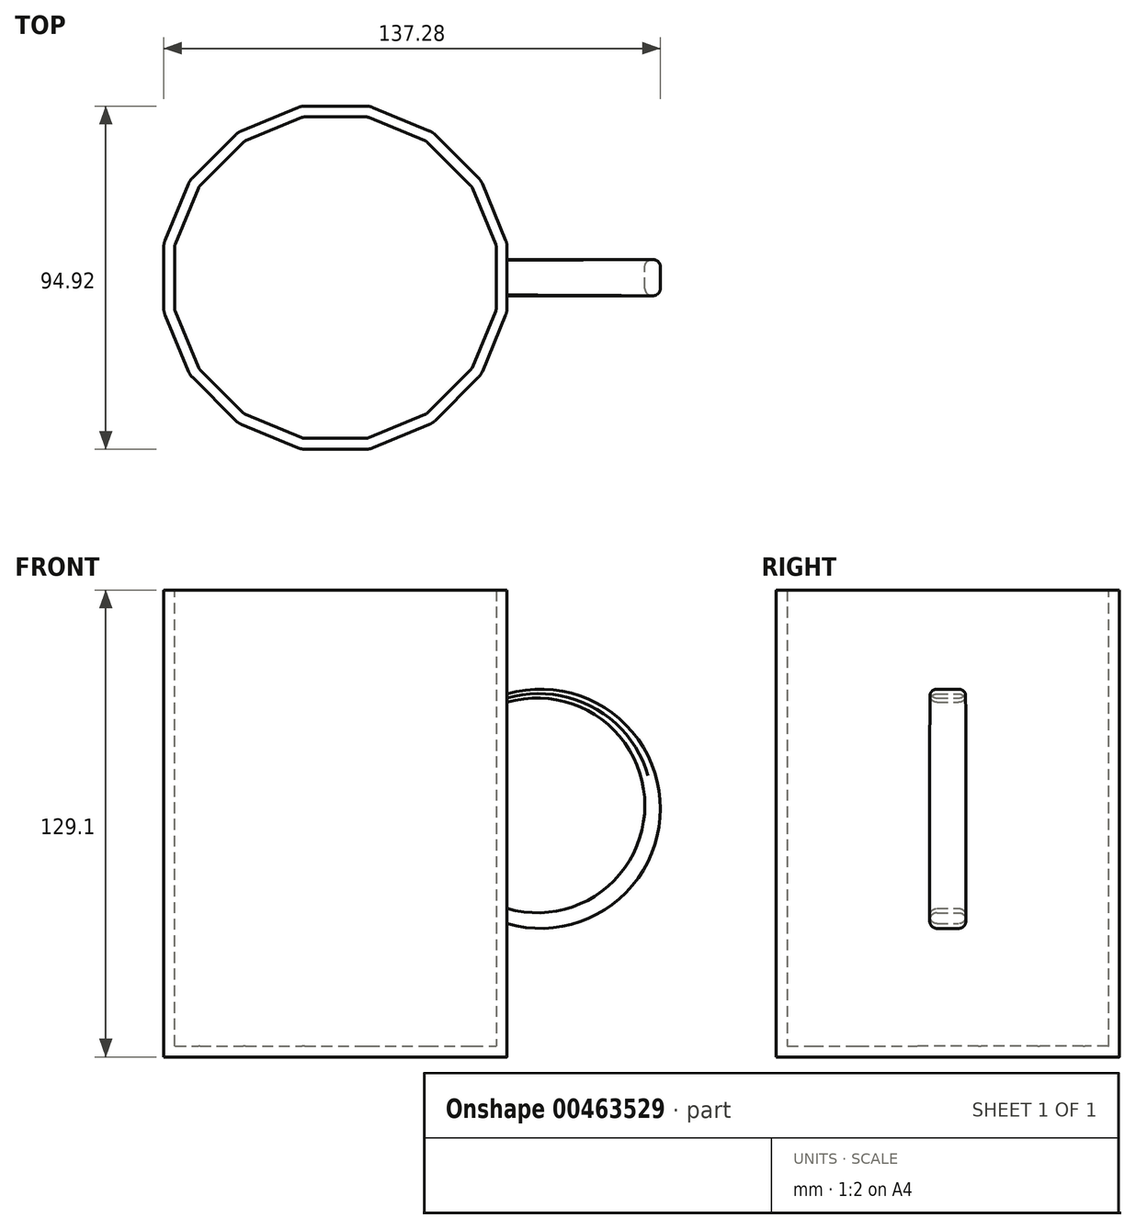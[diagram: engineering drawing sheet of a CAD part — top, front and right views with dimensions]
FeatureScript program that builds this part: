
annotation { "Feature Type Name" : "Feature", "Feature Type Description" : "" }
export const myFeature = defineFeature(function(context is Context, id is Id, definition is map)
    precondition{}
    {
        {
            var Q0;
            Q0=qCreatedBy(makeId("Front.planeOp"),FACE);
            var sketch = newSketch(context, id + "F0", { "sketchPlane" : qUnion([Q0])});
            skArc(sketch, "E0", {"start": v(45.81, 37.4) * mm, "mid": v(89.82, 68.9) * mm, "end": v(45.32, 99.7) * mm});
            skArc(sketch, "E1", {"start": v(46, 41.55) * mm, "mid": v(85.52, 69.91) * mm, "end": v(45.37, 97.38) * mm});
            skLineSegment(sketch, "E2", {"start": v(45.32, 99.7) * mm, "end": v(45.37, 97.38) * mm});
            skLineSegment(sketch, "E3", {"start": v(46, 41.55) * mm, "end": v(45.81, 37.4) * mm});
            skSolve(sketch);
        }
        {
            var Q0;
            Q0=makeQuery(id+"F0.imprint","IMPRINT",FACE,{"disambiguationData":[TD([[makeQuery(id+"F0.imprint","IMPRINT",EDGE,{"derivedFrom":sQuery(id+"F0.wireOp",EDGE,"E0")}),1.0]])]});
            extrude(context, id + "F1", {"entities" : qUnion([Q0]), "endBound" : BoundingType.SYMMETRIC, "depth" : 10 * mm});
        }
        {
            var Q0;
            Q0=qCreatedBy(makeId("Top.planeOp"),FACE);
            var sketch = newSketch(context, id + "F2", { "sketchPlane" : qUnion([Q0])});
            skCircle(sketch, "E4.cCircle", {"center": v(0, 0) * mm, "radius": 47.46 * mm, "construction": true});
            skLineSegment(sketch, "E4.0", {"start": v(47.46, 9.44) * mm, "end": v(47.46, -9.44) * mm});
            skLineSegment(sketch, "E4.1", {"start": v(47.46, -9.44) * mm, "end": v(40.23, -26.88) * mm});
            skLineSegment(sketch, "E4.2", {"start": v(40.23, -26.88) * mm, "end": v(26.88, -40.23) * mm});
            skLineSegment(sketch, "E4.3", {"start": v(26.88, -40.23) * mm, "end": v(9.44, -47.46) * mm});
            skLineSegment(sketch, "E4.4", {"start": v(9.44, -47.46) * mm, "end": v(-9.44, -47.46) * mm});
            skLineSegment(sketch, "E4.5", {"start": v(-9.44, -47.46) * mm, "end": v(-26.88, -40.23) * mm});
            skLineSegment(sketch, "E4.6", {"start": v(-26.88, -40.23) * mm, "end": v(-40.23, -26.88) * mm});
            skLineSegment(sketch, "E4.7", {"start": v(-40.23, -26.88) * mm, "end": v(-47.46, -9.44) * mm});
            skLineSegment(sketch, "E4.8", {"start": v(-47.46, -9.44) * mm, "end": v(-47.46, 9.44) * mm});
            skLineSegment(sketch, "E4.9", {"start": v(-47.46, 9.44) * mm, "end": v(-40.23, 26.88) * mm});
            skLineSegment(sketch, "E4.10", {"start": v(-40.23, 26.88) * mm, "end": v(-26.88, 40.23) * mm});
            skLineSegment(sketch, "E4.11", {"start": v(-26.88, 40.23) * mm, "end": v(-9.44, 47.46) * mm});
            skLineSegment(sketch, "E4.12", {"start": v(-9.44, 47.46) * mm, "end": v(9.44, 47.46) * mm});
            skLineSegment(sketch, "E4.13", {"start": v(9.44, 47.46) * mm, "end": v(26.88, 40.23) * mm});
            skLineSegment(sketch, "E4.14", {"start": v(26.88, 40.23) * mm, "end": v(40.23, 26.88) * mm});
            skLineSegment(sketch, "E4.15", {"start": v(40.23, 26.88) * mm, "end": v(47.46, 9.44) * mm});
            skPoint(sketch, "E4.0.midPoint", {"position": v(47.46, 0) * mm});
            skSolve(sketch);
        }
        {
            var Q0;
            Q0=makeQuery(id+"F2.imprint","IMPRINT",FACE,{"disambiguationData":[TD([[makeQuery(id+"F2.imprint","IMPRINT",EDGE,{"derivedFrom":sQuery(id+"F2.wireOp",EDGE,"E4.0")}),-1.0]])]});
            extrude(context, id + "F3", {"entities" : qUnion([Q0]), "operationType" : NewBodyOperationType.ADD, "depth" : 129.1 * mm});
        }
        {
            var Q0;
            Q0=makeQuery(id+"F3.opExtrude","SWEPT_EDGE",EDGE,{"disambiguationData":[OSD([sQuery(id+"F2.wireOp",EDGE,"E4.6"),sQuery(id+"F2.wireOp",EDGE,"E4.7")])]});
            var Q1;
            Q1=makeQuery(id+"F3.opExtrude","SWEPT_EDGE",EDGE,{"disambiguationData":[OSD([sQuery(id+"F2.wireOp",EDGE,"E4.7"),sQuery(id+"F2.wireOp",EDGE,"E4.8")])]});
            var Q2;
            Q2=makeQuery(id+"F3.opExtrude","SWEPT_EDGE",EDGE,{"disambiguationData":[OSD([sQuery(id+"F2.wireOp",EDGE,"E4.8"),sQuery(id+"F2.wireOp",EDGE,"E4.9")])]});
            var Q3;
            Q3=makeQuery(id+"F3.opExtrude","SWEPT_EDGE",EDGE,{"disambiguationData":[OSD([sQuery(id+"F2.wireOp",EDGE,"E4.9"),sQuery(id+"F2.wireOp",EDGE,"E4.10")])]});
            var Q4;
            Q4=makeQuery(id+"F3.opExtrude","SWEPT_EDGE",EDGE,{"disambiguationData":[OSD([sQuery(id+"F2.wireOp",EDGE,"E4.10"),sQuery(id+"F2.wireOp",EDGE,"E4.11")])]});
            var Q5;
            Q5=makeQuery(id+"F3.opExtrude","SWEPT_EDGE",EDGE,{"disambiguationData":[OSD([sQuery(id+"F2.wireOp",EDGE,"E4.11"),sQuery(id+"F2.wireOp",EDGE,"E4.12")])]});
            var Q6;
            Q6=makeQuery(id+"F3.opExtrude","SWEPT_EDGE",EDGE,{"disambiguationData":[OSD([sQuery(id+"F2.wireOp",EDGE,"E4.12"),sQuery(id+"F2.wireOp",EDGE,"E4.13")])]});
            var Q7;
            Q7=makeQuery(id+"F3.opExtrude","SWEPT_EDGE",EDGE,{"disambiguationData":[OSD([sQuery(id+"F2.wireOp",EDGE,"E4.13"),sQuery(id+"F2.wireOp",EDGE,"E4.14")])]});
            var Q8;
            Q8=makeQuery(id+"F3.opExtrude","SWEPT_EDGE",EDGE,{"disambiguationData":[OSD([sQuery(id+"F2.wireOp",EDGE,"E4.14"),sQuery(id+"F2.wireOp",EDGE,"E4.15")])]});
            var Q9;
            Q9=makeQuery(id+"F3.opExtrude","SWEPT_EDGE",EDGE,{"disambiguationData":[OSD([sQuery(id+"F2.wireOp",EDGE,"E4.0"),sQuery(id+"F2.wireOp",EDGE,"E4.15")])]});
            var Q10;
            Q10=makeQuery(id+"F3.opExtrude","SWEPT_EDGE",EDGE,{"disambiguationData":[OSD([sQuery(id+"F2.wireOp",EDGE,"E4.0"),sQuery(id+"F2.wireOp",EDGE,"E4.1")])]});
            var Q11;
            Q11=makeQuery(id+"F3.opExtrude","SWEPT_EDGE",EDGE,{"disambiguationData":[OSD([sQuery(id+"F2.wireOp",EDGE,"E4.3"),sQuery(id+"F2.wireOp",EDGE,"E4.4")])]});
            var Q12;
            Q12=makeQuery(id+"F3.opExtrude","SWEPT_EDGE",EDGE,{"disambiguationData":[OSD([sQuery(id+"F2.wireOp",EDGE,"E4.2"),sQuery(id+"F2.wireOp",EDGE,"E4.3")])]});
            var Q13;
            Q13=makeQuery(id+"F3.opExtrude","SWEPT_EDGE",EDGE,{"disambiguationData":[OSD([sQuery(id+"F2.wireOp",EDGE,"E4.1"),sQuery(id+"F2.wireOp",EDGE,"E4.2")])]});
            var Q14;
            Q14=makeQuery(id+"F3.opExtrude","SWEPT_EDGE",EDGE,{"disambiguationData":[OSD([sQuery(id+"F2.wireOp",EDGE,"E4.5"),sQuery(id+"F2.wireOp",EDGE,"E4.6")])]});
            var Q15;
            Q15=makeQuery(id+"F3.opExtrude","SWEPT_EDGE",EDGE,{"disambiguationData":[OSD([sQuery(id+"F2.wireOp",EDGE,"E4.4"),sQuery(id+"F2.wireOp",EDGE,"E4.5")])]});
            fillet(context, id + "F4", {"entities" : qUnion([Q0, Q1, Q2, Q3, Q4, Q5, Q6, Q7, Q8, Q9, Q10, Q11, Q12, Q13, Q14, Q15]), "radius" : 5 * mm, "tangentPropagation" : true, "allowEdgeOverflow" : false});
        }
        {
            var Q0;
            Q0=makeQuery(id+"F1.opExtrude","CAP_EDGE",EDGE,{"disambiguationData":[OSD([sQuery(id+"F0.wireOp",EDGE,"E0")])],"isStart":false});
            var Q1;
            Q1=makeQuery(id+"F1.opExtrude","CAP_EDGE",EDGE,{"disambiguationData":[OSD([sQuery(id+"F0.wireOp",EDGE,"E1")])],"isStart":true});
            var Q2;
            Q2=makeQuery(id+"F1.opExtrude","CAP_EDGE",EDGE,{"disambiguationData":[OSD([sQuery(id+"F0.wireOp",EDGE,"E1")])],"isStart":false});
            var Q3;
            Q3=makeQuery(id+"F1.opExtrude","CAP_EDGE",EDGE,{"disambiguationData":[OSD([sQuery(id+"F0.wireOp",EDGE,"E0")])],"isStart":true});
            fillet(context, id + "F5", {"entities" : qUnion([Q0, Q1, Q2, Q3]), "radius" : 2 * mm, "tangentPropagation" : true, "allowEdgeOverflow" : false});
        }
        {
            var Q0;
            Q0=makeQuery(id+"F3.opExtrude","CAP_FACE",FACE,{"disambiguationData":[OSD([sQuery(id+"F2.wireOp",EDGE,"E4.0"),sQuery(id+"F2.wireOp",EDGE,"E4.1"),sQuery(id+"F2.wireOp",EDGE,"E4.2"),sQuery(id+"F2.wireOp",EDGE,"E4.3"),sQuery(id+"F2.wireOp",EDGE,"E4.4"),sQuery(id+"F2.wireOp",EDGE,"E4.5"),sQuery(id+"F2.wireOp",EDGE,"E4.6"),sQuery(id+"F2.wireOp",EDGE,"E4.7"),sQuery(id+"F2.wireOp",EDGE,"E4.8"),sQuery(id+"F2.wireOp",EDGE,"E4.9"),sQuery(id+"F2.wireOp",EDGE,"E4.10"),sQuery(id+"F2.wireOp",EDGE,"E4.11"),sQuery(id+"F2.wireOp",EDGE,"E4.12"),sQuery(id+"F2.wireOp",EDGE,"E4.13"),sQuery(id+"F2.wireOp",EDGE,"E4.14"),sQuery(id+"F2.wireOp",EDGE,"E4.15")])],"isStart":false});
            shell(context, id + "F6", {"entities" : qUnion([Q0]), "thickness" : 3 * mm});
        }
    });
